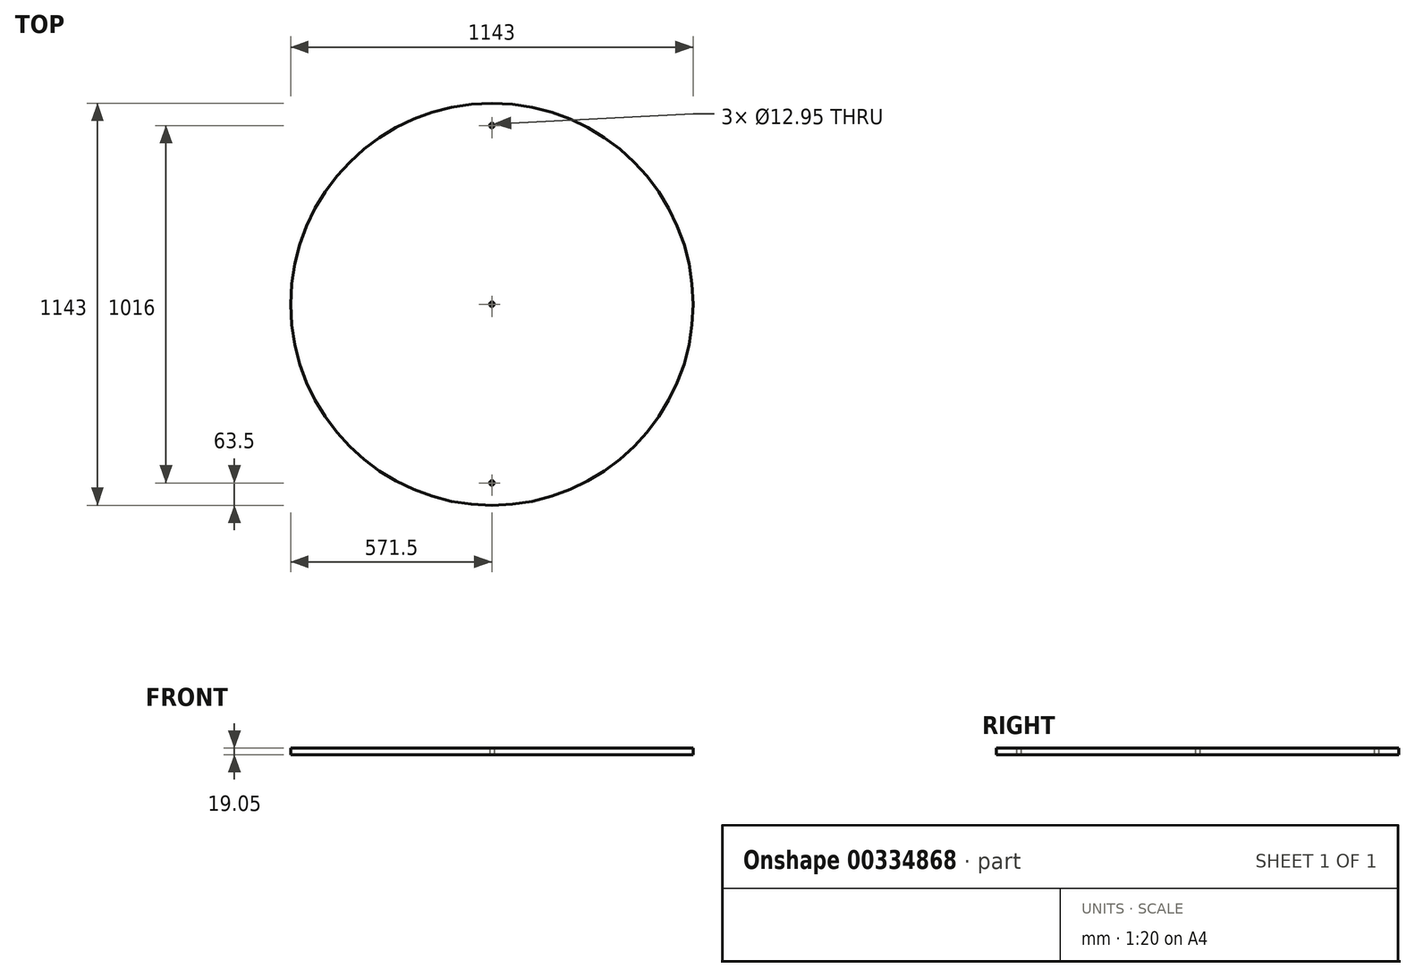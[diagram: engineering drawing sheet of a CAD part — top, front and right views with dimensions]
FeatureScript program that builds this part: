
annotation { "Feature Type Name" : "Feature", "Feature Type Description" : "" }
export const myFeature = defineFeature(function(context is Context, id is Id, definition is map)
    precondition{}
    {
        {
            var Q0;
            Q0=qCreatedBy(makeId("Top.planeOp"),FACE);
            var sketch = newSketch(context, id + "F0", { "sketchPlane" : qUnion([Q0])});
            skCircle(sketch, "E0", {"center": v(0, 0) * mm, "radius": 571.5 * mm});
            skCircle(sketch, "E1", {"center": v(0, -508) * mm, "radius": 6.48 * mm});
            skCircle(sketch, "E2", {"center": v(0, 508) * mm, "radius": 6.48 * mm});
            skCircle(sketch, "E3", {"center": v(0, 0) * mm, "radius": 6.48 * mm});
            skPoint(sketch, "E4", {"position": v(484.1, 225.63) * mm});
            skSolve(sketch);
        }
        {
            var Q0;
            Q0=makeQuery(id+"F0.imprint","IMPRINT",FACE,{"disambiguationData":[TD([[makeQuery(id+"F0.imprint","IMPRINT",EDGE,{"derivedFrom":sQuery(id+"F0.wireOp",EDGE,"E0")}),1.0]])]});
            extrude(context, id + "F1", {"entities" : qUnion([Q0]), "depth" : 19.05 * mm});
        }
    });
